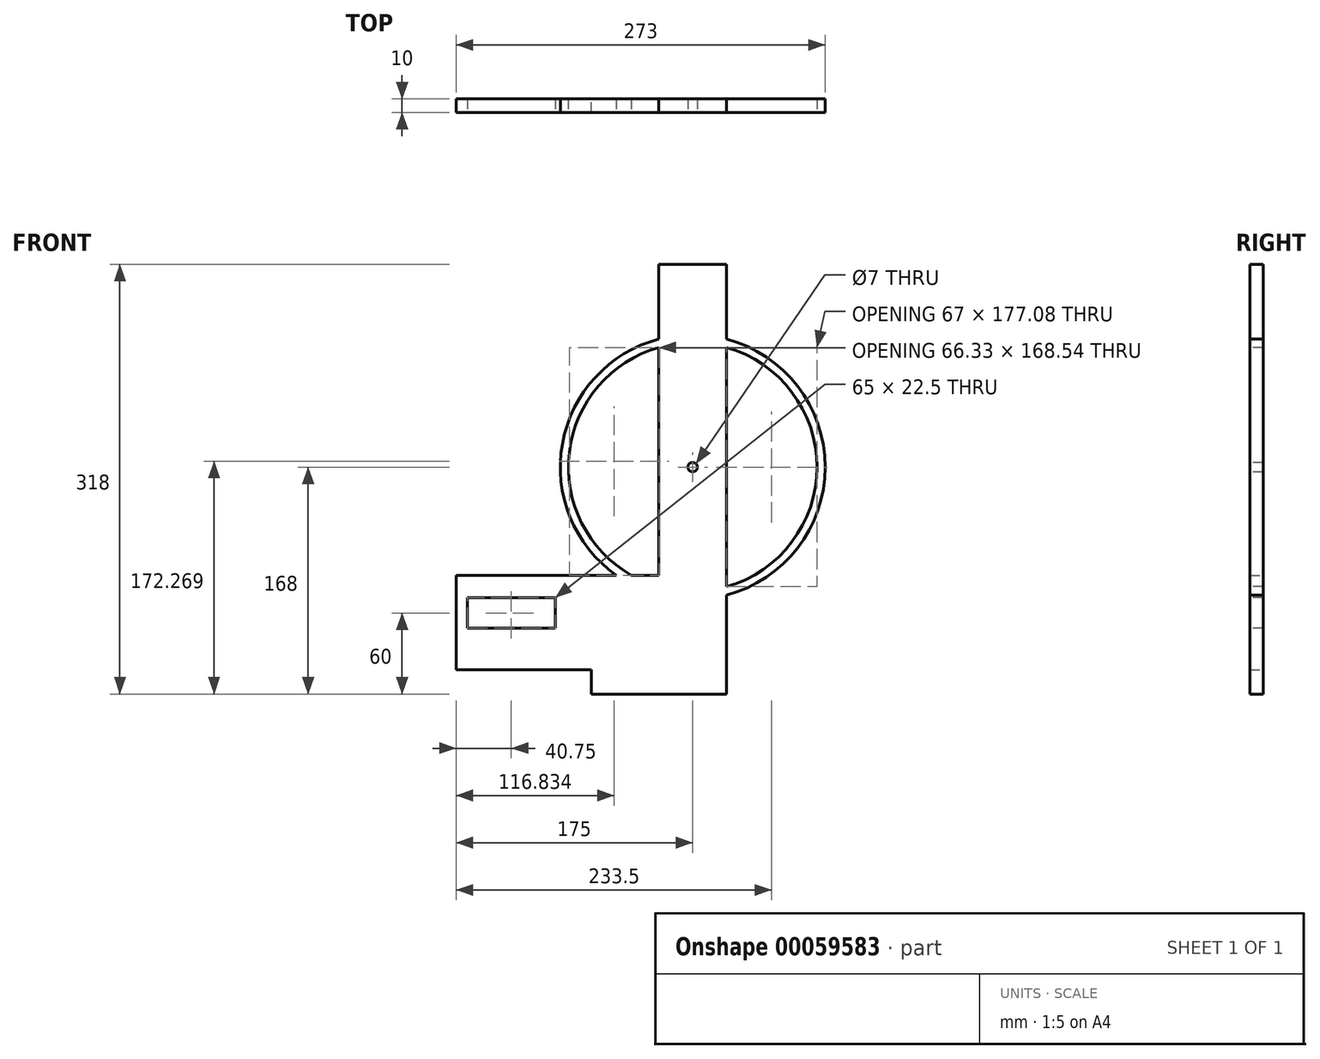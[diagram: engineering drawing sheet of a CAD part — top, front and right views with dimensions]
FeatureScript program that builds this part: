
annotation { "Feature Type Name" : "Feature", "Feature Type Description" : "" }
export const myFeature = defineFeature(function(context is Context, id is Id, definition is map)
    precondition{}
    {
        {
            var Q0;
            Q0=qCreatedBy(makeId("Front.planeOp"),FACE);
            var sketch = newSketch(context, id + "F0", { "sketchPlane" : qUnion([Q0])});
            skLineSegment(sketch, "E0.bottom", {"start": v(-25, 150) * mm, "end": v(25, 150) * mm});
            skLineSegment(sketch, "E0.top", {"start": v(-25, -150) * mm, "end": v(25, -150) * mm});
            skLineSegment(sketch, "E0.left", {"start": v(-25, 150) * mm, "end": v(-25, -150) * mm});
            skLineSegment(sketch, "E0.right", {"start": v(25, 150) * mm, "end": v(25, -150) * mm});
            skPoint(sketch, "E0.middle", {"position": v(0, 0) * mm});
            skLineSegment(sketch, "E1.bottom", {"start": v(-25, -150) * mm, "end": v(-175, -150) * mm});
            skLineSegment(sketch, "E1.top", {"start": v(-25, -80) * mm, "end": v(-175, -80) * mm});
            skLineSegment(sketch, "E1.left", {"start": v(-25, -150) * mm, "end": v(-25, -80) * mm});
            skLineSegment(sketch, "E1.right", {"start": v(-175, -150) * mm, "end": v(-175, -80) * mm});
            skSolve(sketch);
        }
        {
            var Q0;
            Q0=qSketchRegion(id+"F0",true);
            extrude(context, id + "F1", {"entities" : qUnion([Q0]), "depth" : 10 * mm});
        }
        {
            var Q0;
            Q0=makeQuery(id+"F1.opExtrude","CAP_FACE",FACE,{"disambiguationData":[OSD([sQuery(id+"F0.wireOp",EDGE,"E0.bottom"),sQuery(id+"F0.wireOp",EDGE,"E0.top"),sQuery(id+"F0.wireOp",EDGE,"E0.left"),sQuery(id+"F0.wireOp",EDGE,"E0.right"),sQuery(id+"F0.wireOp",EDGE,"E1.bottom"),sQuery(id+"F0.wireOp",EDGE,"E1.top"),sQuery(id+"F0.wireOp",EDGE,"E1.right")])],"isStart":false});
            var sketch = newSketch(context, id + "F2", { "sketchPlane" : qUnion([Q0])});
            skCircle(sketch, "E2", {"center": v(0, 0) * mm, "radius": 125 * mm, "construction": true});
            skCircle(sketch, "E3", {"center": v(0, 0) * mm, "radius": 95 * mm, "construction": true});
            skCircle(sketch, "E4", {"center": v(0, 0) * mm, "radius": 98 * mm});
            skCircle(sketch, "E5", {"center": v(0, 0) * mm, "radius": 92 * mm});
            skSolve(sketch);
        }
        {
            var Q0;
            Q0=qSketchRegion(id+"F2",true);
            extrude(context, id + "F3", {"entities" : qUnion([Q0]), "operationType" : NewBodyOperationType.ADD, "oppositeDirection" : true, "depth" : 10 * mm});
        }
        {
            var Q0;
            Q0=makeQuery(id+"F1.opExtrude","SWEPT_FACE",FACE,{"disambiguationData":[OSD([sQuery(id+"F0.wireOp",EDGE,"E0.top"),sQuery(id+"F0.wireOp",EDGE,"E1.bottom")])]});
            var sketch = newSketch(context, id + "F4", { "sketchPlane" : qUnion([Q0])});
            skLineSegment(sketch, "E6.bottom", {"start": v(25, 10) * mm, "end": v(-75, 10) * mm});
            skLineSegment(sketch, "E6.top", {"start": v(25, 0) * mm, "end": v(-75, 0) * mm});
            skLineSegment(sketch, "E6.left", {"start": v(25, 10) * mm, "end": v(25, 0) * mm});
            skLineSegment(sketch, "E6.right", {"start": v(-75, 10) * mm, "end": v(-75, 0) * mm});
            skSolve(sketch);
        }
        {
            var Q0;
            Q0=qSketchRegion(id+"F4",true);
            extrude(context, id + "F5", {"entities" : qUnion([Q0]), "operationType" : NewBodyOperationType.ADD, "depth" : 18 * mm});
        }
        {
            var Q0;
            Q0=makeQuery(id+"F5.boolean.opBoolean","MERGE",FACE,{"derivedFrom":[makeQuery(id+"F3.boolean.opBoolean","MERGE",FACE,{"derivedFrom":[makeQuery(id+"F1.opExtrude","CAP_FACE",FACE,{"disambiguationData":[OSD([sQuery(id+"F0.wireOp",EDGE,"E0.bottom"),sQuery(id+"F0.wireOp",EDGE,"E0.top"),sQuery(id+"F0.wireOp",EDGE,"E0.left"),sQuery(id+"F0.wireOp",EDGE,"E0.right"),sQuery(id+"F0.wireOp",EDGE,"E1.bottom"),sQuery(id+"F0.wireOp",EDGE,"E1.top"),sQuery(id+"F0.wireOp",EDGE,"E1.right")])],"isStart":false}),makeQuery(id+"F3.opExtrude","CAP_FACE",FACE,{"disambiguationData":[OSD([sQuery(id+"F2.wireOp",EDGE,"E4"),sQuery(id+"F2.wireOp",EDGE,"E5")])],"isStart":true})]}),makeQuery(id+"F5.opExtrude","SWEPT_FACE",FACE,{"disambiguationData":[OSD([sQuery(id+"F4.wireOp",EDGE,"BhvBbVAg-w6V3-QJHI-VM8m-rcusInK2M3kt.bottom")])]})]});
            var sketch = newSketch(context, id + "F6", { "sketchPlane" : qUnion([Q0])});
            skCircle(sketch, "E7", {"center": v(0, 0) * mm, "radius": 3.5 * mm});
            skSolve(sketch);
        }
        {
            var Q0;
            Q0=qSketchRegion(id+"F6",true);
            extrude(context, id + "F7", {"entities" : qUnion([Q0]), "operationType" : NewBodyOperationType.REMOVE, "oppositeDirection" : true, "depth" : 25 * mm});
        }
        {
            var Q0;
            Q0=makeQuery(id+"F5.boolean.opBoolean","MERGE",FACE,{"derivedFrom":[makeQuery(id+"F3.boolean.opBoolean","MERGE",FACE,{"derivedFrom":[makeQuery(id+"F1.opExtrude","CAP_FACE",FACE,{"disambiguationData":[OSD([sQuery(id+"F0.wireOp",EDGE,"E0.bottom"),sQuery(id+"F0.wireOp",EDGE,"E0.top"),sQuery(id+"F0.wireOp",EDGE,"E0.left"),sQuery(id+"F0.wireOp",EDGE,"E0.right"),sQuery(id+"F0.wireOp",EDGE,"E1.bottom"),sQuery(id+"F0.wireOp",EDGE,"E1.top"),sQuery(id+"F0.wireOp",EDGE,"E1.right")])],"isStart":false}),makeQuery(id+"F3.opExtrude","CAP_FACE",FACE,{"disambiguationData":[OSD([sQuery(id+"F2.wireOp",EDGE,"E4"),sQuery(id+"F2.wireOp",EDGE,"E5")])],"isStart":true})]}),makeQuery(id+"F5.opExtrude","SWEPT_FACE",FACE,{"disambiguationData":[OSD([sQuery(id+"F4.wireOp",EDGE,"E6.bottom")])]})]});
            var sketch = newSketch(context, id + "F8", { "sketchPlane" : qUnion([Q0])});
            skCircle(sketch, "E8", {"center": v(-113, -108) * mm, "radius": 3.5 * mm});
            skSolve(sketch);
        }
        {
            var Q0;
            Q0 = qSketchRegion(id + "F8", true);
            extrude(context, id + "F9", {"entities" : qUnion([Q0]), "operationType" : NewBodyOperationType.REMOVE, "oppositeDirection" : true, "depth" : 25 * mm});
        }
        {
            var Q0;
            Q0=makeQuery(id+"F5.boolean.opBoolean","MERGE",FACE,{"derivedFrom":[makeQuery(id+"F3.boolean.opBoolean","MERGE",FACE,{"derivedFrom":[makeQuery(id+"F1.opExtrude","CAP_FACE",FACE,{"disambiguationData":[OSD([sQuery(id+"F0.wireOp",EDGE,"E0.bottom"),sQuery(id+"F0.wireOp",EDGE,"E0.top"),sQuery(id+"F0.wireOp",EDGE,"E0.left"),sQuery(id+"F0.wireOp",EDGE,"E0.right"),sQuery(id+"F0.wireOp",EDGE,"E1.bottom"),sQuery(id+"F0.wireOp",EDGE,"E1.top"),sQuery(id+"F0.wireOp",EDGE,"E1.right")])],"isStart":false}),makeQuery(id+"F3.opExtrude","CAP_FACE",FACE,{"disambiguationData":[OSD([sQuery(id+"F2.wireOp",EDGE,"E4"),sQuery(id+"F2.wireOp",EDGE,"E5")])],"isStart":true})]}),makeQuery(id+"F5.opExtrude","SWEPT_FACE",FACE,{"disambiguationData":[OSD([sQuery(id+"F4.wireOp",EDGE,"E6.bottom")])]})]});
            var sketch = newSketch(context, id + "F10", { "sketchPlane" : qUnion([Q0])});
            skLineSegment(sketch, "E9.bottom", {"start": v(-166.75, -96.75) * mm, "end": v(-101.75, -96.75) * mm});
            skLineSegment(sketch, "E9.top", {"start": v(-166.75, -119.25) * mm, "end": v(-101.75, -119.25) * mm});
            skLineSegment(sketch, "E9.left", {"start": v(-166.75, -96.75) * mm, "end": v(-166.75, -119.25) * mm});
            skLineSegment(sketch, "E9.right", {"start": v(-101.75, -96.75) * mm, "end": v(-101.75, -119.25) * mm});
            skCircle(sketch, "E10", {"center": v(-113, -108) * mm, "radius": 3.5 * mm, "construction": true});
            skSolve(sketch);
        }
        {
            var Q0;
            Q0 = qSketchRegion(id + "F10", true);
            extrude(context, id + "F11", {"entities" : qUnion([Q0]), "operationType" : NewBodyOperationType.REMOVE, "oppositeDirection" : true, "depth" : 25 * mm});
        }
    });
